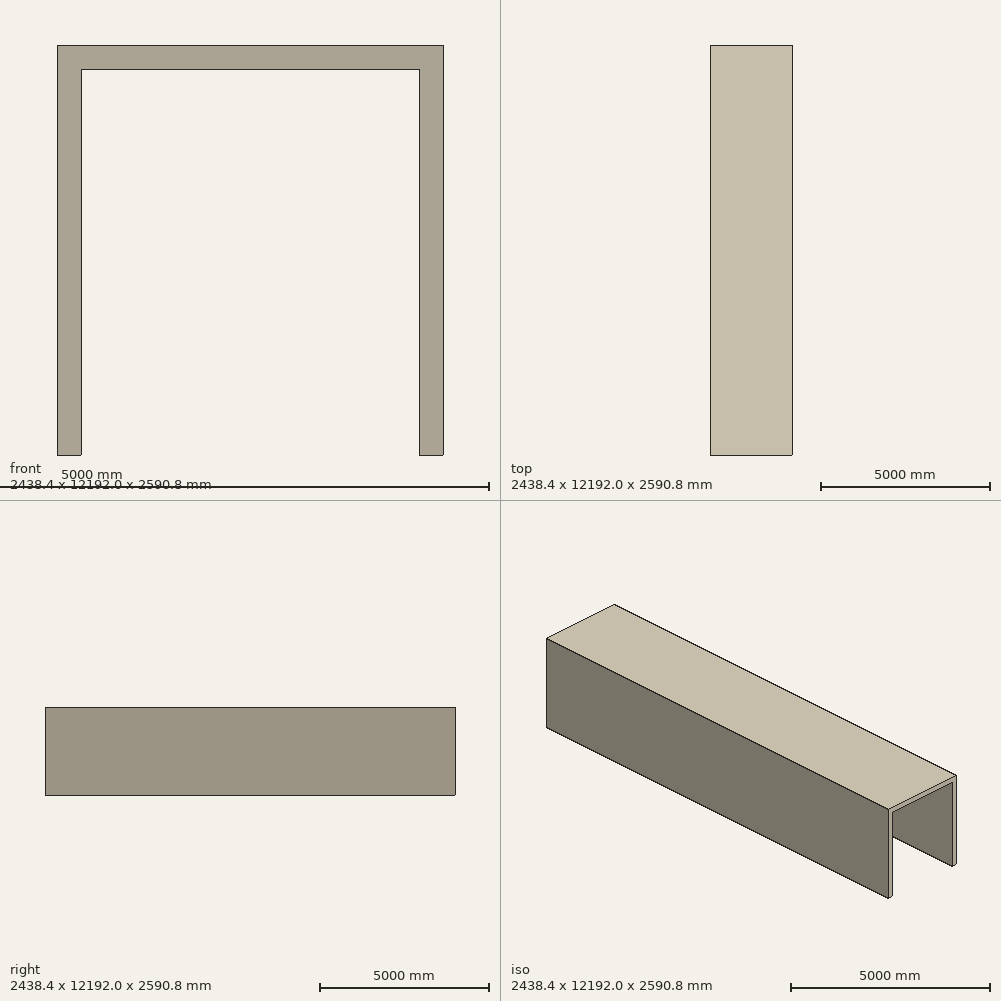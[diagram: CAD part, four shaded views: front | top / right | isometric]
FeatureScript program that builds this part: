
annotation { "Feature Type Name" : "Feature", "Feature Type Description" : "" }
export const myFeature = defineFeature(function(context is Context, id is Id, definition is map)
    precondition{}
    {
        {
            var Q0;
            Q0=qCreatedBy(makeId("Front.planeOp"),FACE);
            var sketch = newSketch(context, id + "F0", { "sketchPlane" : qUnion([Q0])});
            skLineSegment(sketch, "E0.bottom", {"start": v(0, 0) * mm, "end": v(2438.4, 0) * mm});
            skLineSegment(sketch, "E0.top", {"start": v(0, 2590.8) * mm, "end": v(2438.4, 2590.8) * mm});
            skLineSegment(sketch, "E0.left", {"start": v(0, 0) * mm, "end": v(0, 2590.8) * mm});
            skLineSegment(sketch, "E0.right", {"start": v(2438.4, 0) * mm, "end": v(2438.4, 2590.8) * mm});
            skSolve(sketch);
        }
        {
            var Q0;
            Q0 = qSketchRegion(id + "F0", true);
            extrude(context, id + "F1", {"entities" : qUnion([Q0]), "depth" : 12192 * mm});
        }
        {
            var Q0;
            Q0=makeQuery(id+"F1.opExtrude","CAP_FACE",FACE,{"disambiguationData":[OSD([sQuery(id+"F0.wireOp",EDGE,"E0.bottom"),sQuery(id+"F0.wireOp",EDGE,"E0.top"),sQuery(id+"F0.wireOp",EDGE,"E0.left"),sQuery(id+"F0.wireOp",EDGE,"E0.right")])],"isStart":false});
            var sketch = newSketch(context, id + "F2", { "sketchPlane" : qUnion([Q0])});
            skLineSegment(sketch, "E1.bottom", {"start": v(152.4, 0) * mm, "end": v(2286, 0) * mm});
            skLineSegment(sketch, "E1.top", {"start": v(152.4, 2438.4) * mm, "end": v(2286, 2438.4) * mm});
            skLineSegment(sketch, "E1.left", {"start": v(152.4, 0) * mm, "end": v(152.4, 2438.4) * mm});
            skLineSegment(sketch, "E1.right", {"start": v(2286, 0) * mm, "end": v(2286, 2438.4) * mm});
            skSolve(sketch);
        }
        {
            var Q0;
            Q0 = qSketchRegion(id + "F2", true);
            extrude(context, id + "F3", {"entities" : qUnion([Q0]), "operationType" : NewBodyOperationType.REMOVE, "endBound" : BoundingType.THROUGH_ALL, "oppositeDirection" : true, "depth" : 25.4 * mm});
        }
    });
